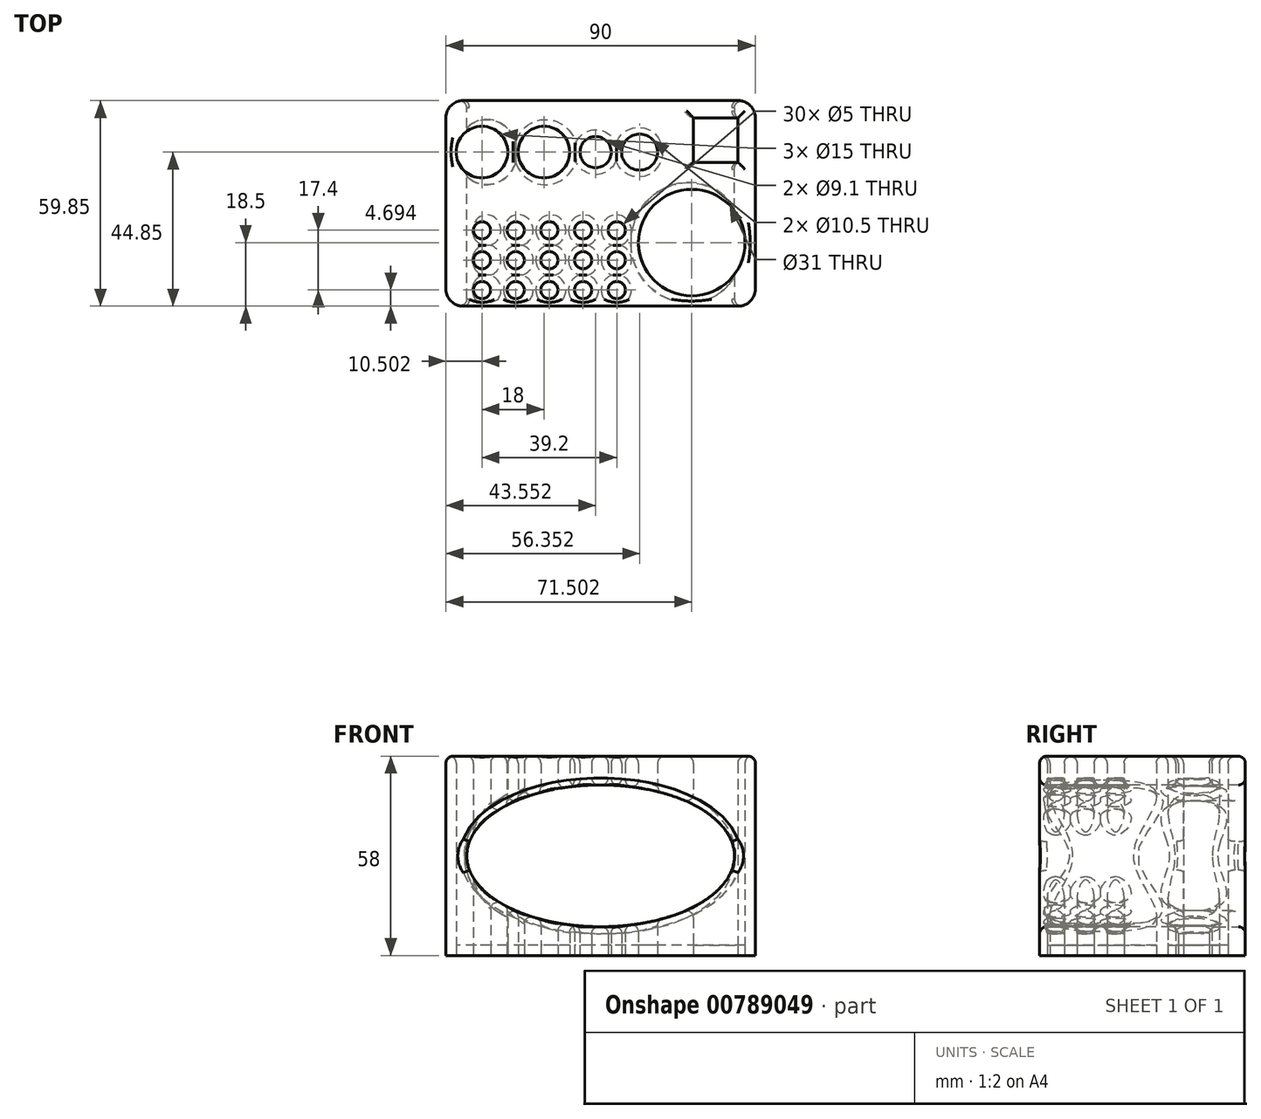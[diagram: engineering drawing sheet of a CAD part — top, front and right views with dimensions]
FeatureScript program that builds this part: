
annotation { "Feature Type Name" : "Feature", "Feature Type Description" : "" }
export const myFeature = defineFeature(function(context is Context, id is Id, definition is map)
    precondition{}
    {
        {
            var Q0;
            Q0=qCreatedBy(makeId("Top.planeOp"),FACE);
            var sketch = newSketch(context, id + "F0", { "sketchPlane" : qUnion([Q0])});
            skLineSegment(sketch, "E0.bottom", {"start": v(-28.22, 30.72) * mm, "end": v(51.78, 30.72) * mm});
            skLineSegment(sketch, "E0.top", {"start": v(-28.22, -29.13) * mm, "end": v(51.78, -29.13) * mm});
            skLineSegment(sketch, "E0.left", {"start": v(-33.22, 25.72) * mm, "end": v(-33.22, -24.13) * mm});
            skLineSegment(sketch, "E0.right", {"start": v(56.78, 25.72) * mm, "end": v(56.78, -24.13) * mm});
            skLineSegment(sketch, "E1.bottom", {"start": v(38.78, 25.72) * mm, "end": v(51.78, 25.72) * mm});
            skLineSegment(sketch, "E1.top", {"start": v(38.78, 12.72) * mm, "end": v(51.78, 12.72) * mm});
            skLineSegment(sketch, "E1.left", {"start": v(38.78, 25.72) * mm, "end": v(38.78, 12.72) * mm});
            skLineSegment(sketch, "E1.right", {"start": v(51.78, 25.72) * mm, "end": v(51.78, 12.72) * mm});
            skCircle(sketch, "E2", {"center": v(38.28, -10.63) * mm, "radius": 15.5 * mm});
            skCircle(sketch, "E3", {"center": v(-22.72, 15.72) * mm, "radius": 7.5 * mm});
            skCircle(sketch, "E4", {"center": v(-4.72, 15.72) * mm, "radius": 7.5 * mm});
            skLineSegment(sketch, "E5", {"start": v(-22.72, 15.72) * mm, "end": v(55.26, 15.72) * mm, "construction": true});
            skCircle(sketch, "E6", {"center": v(10.33, 15.72) * mm, "radius": 4.55 * mm});
            skCircle(sketch, "E7", {"center": v(23.13, 15.72) * mm, "radius": 5.25 * mm});
            skCircle(sketch, "E8", {"center": v(-22.72, -7.04) * mm, "radius": 2.5 * mm});
            skLineSegment(sketch, "E9", {"start": v(-22.72, 15.72) * mm, "end": v(-22.72, -24.26) * mm, "construction": true});
            skCircle(sketch, "E10.0.1.0", {"center": v(-22.72, -15.74) * mm, "radius": 2.5 * mm});
            skCircle(sketch, "E10.0.2.0", {"center": v(-22.72, -24.44) * mm, "radius": 2.5 * mm});
            skCircle(sketch, "E10.1.0.0", {"center": v(-12.92, -7.04) * mm, "radius": 2.5 * mm});
            skCircle(sketch, "E10.1.1.0", {"center": v(-12.92, -15.74) * mm, "radius": 2.5 * mm});
            skCircle(sketch, "E10.1.2.0", {"center": v(-12.92, -24.44) * mm, "radius": 2.5 * mm});
            skCircle(sketch, "E10.2.0.0", {"center": v(-3.12, -7.04) * mm, "radius": 2.5 * mm});
            skCircle(sketch, "E10.2.1.0", {"center": v(-3.12, -15.74) * mm, "radius": 2.5 * mm});
            skCircle(sketch, "E10.2.2.0", {"center": v(-3.12, -24.44) * mm, "radius": 2.5 * mm});
            skCircle(sketch, "E10.3.0.0", {"center": v(6.68, -7.04) * mm, "radius": 2.5 * mm});
            skCircle(sketch, "E10.3.1.0", {"center": v(6.68, -15.74) * mm, "radius": 2.5 * mm});
            skCircle(sketch, "E10.3.2.0", {"center": v(6.68, -24.44) * mm, "radius": 2.5 * mm});
            skCircle(sketch, "E10.4.0.0", {"center": v(16.48, -7.04) * mm, "radius": 2.5 * mm});
            skCircle(sketch, "E10.4.1.0", {"center": v(16.48, -15.74) * mm, "radius": 2.5 * mm});
            skCircle(sketch, "E10.4.2.0", {"center": v(16.48, -24.44) * mm, "radius": 2.5 * mm});
            skLineSegment(sketch, "E10.direction1", {"start": v(-22.72, -7.04) * mm, "end": v(-12.92, -7.04) * mm, "construction": true});
            skLineSegment(sketch, "E10.direction2", {"start": v(-22.72, -7.04) * mm, "end": v(-22.72, -15.74) * mm, "construction": true});
            skPoint(sketch, "E11.visualSharp", {"position": v(-33.22, 30.72) * mm});
            skArc(sketch, "E11.filletArc", {"start": v(-28.22, 30.72) * mm, "mid": v(-31.75, 29.26) * mm, "end": v(-33.22, 25.72) * mm});
            skPoint(sketch, "E12.visualSharp", {"position": v(56.78, 30.72) * mm});
            skArc(sketch, "E12.filletArc", {"start": v(56.78, 25.72) * mm, "mid": v(55.32, 29.26) * mm, "end": v(51.78, 30.72) * mm});
            skPoint(sketch, "E13.visualSharp", {"position": v(56.78, -29.13) * mm});
            skArc(sketch, "E13.filletArc", {"start": v(51.78, -29.13) * mm, "mid": v(55.32, -27.67) * mm, "end": v(56.78, -24.13) * mm});
            skPoint(sketch, "E14.visualSharp", {"position": v(-33.22, -29.13) * mm});
            skArc(sketch, "E14.filletArc", {"start": v(-33.22, -24.13) * mm, "mid": v(-31.75, -27.67) * mm, "end": v(-28.22, -29.13) * mm});
            skSolve(sketch);
        }
        {
            var Q0;
            Q0=makeQuery(id+"F0.imprint","IMPRINT",FACE,{"disambiguationData":[TD([[makeQuery(id+"F0.imprint","IMPRINT",EDGE,{"derivedFrom":sQuery(id+"F0.wireOp",EDGE,"E0.bottom")}),-1.0]])]});
            extrude(context, id + "F1", {"entities" : qUnion([Q0]), "depth" : 58 * mm, "offsetDistance" : 25 * mm});
        }
        {
            var Q0;
            Q0=makeQuery(id+"F0.imprint","IMPRINT",FACE,{"disambiguationData":[TD([[makeQuery(id+"F0.imprint","IMPRINT",EDGE,{"derivedFrom":sQuery(id+"F0.wireOp",EDGE,"E3")}),1.0]])]});
            var Q1;
            Q1=makeQuery(id+"F0.imprint","IMPRINT",FACE,{"disambiguationData":[TD([[makeQuery(id+"F0.imprint","IMPRINT",EDGE,{"derivedFrom":sQuery(id+"F0.wireOp",EDGE,"E4")}),1.0]])]});
            var Q2;
            Q2=makeQuery(id+"F0.imprint","IMPRINT",FACE,{"disambiguationData":[TD([[makeQuery(id+"F0.imprint","IMPRINT",EDGE,{"derivedFrom":sQuery(id+"F0.wireOp",EDGE,"E6")}),1.0]])]});
            var Q3;
            Q3=makeQuery(id+"F0.imprint","IMPRINT",FACE,{"disambiguationData":[TD([[makeQuery(id+"F0.imprint","IMPRINT",EDGE,{"derivedFrom":sQuery(id+"F0.wireOp",EDGE,"E7")}),1.0]])]});
            var Q4;
            Q4=makeQuery(id+"F0.imprint","IMPRINT",FACE,{"disambiguationData":[TD([[makeQuery(id+"F0.imprint","IMPRINT",EDGE,{"derivedFrom":sQuery(id+"F0.wireOp",EDGE,"E1.bottom")}),-1.0]])]});
            var Q5;
            Q5=makeQuery(id+"F0.imprint","IMPRINT",FACE,{"disambiguationData":[TD([[makeQuery(id+"F0.imprint","IMPRINT",EDGE,{"derivedFrom":sQuery(id+"F0.wireOp",EDGE,"E2")}),1.0]])]});
            var Q6;
            Q6=makeQuery(id+"F0.imprint","IMPRINT",FACE,{"disambiguationData":[TD([[makeQuery(id+"F0.imprint","IMPRINT",EDGE,{"derivedFrom":sQuery(id+"F0.wireOp",EDGE,"E10.4.0.0")}),1.0]])]});
            var Q7;
            Q7=makeQuery(id+"F0.imprint","IMPRINT",FACE,{"disambiguationData":[TD([[makeQuery(id+"F0.imprint","IMPRINT",EDGE,{"derivedFrom":sQuery(id+"F0.wireOp",EDGE,"E10.4.1.0")}),1.0]])]});
            var Q8;
            Q8=makeQuery(id+"F0.imprint","IMPRINT",FACE,{"disambiguationData":[TD([[makeQuery(id+"F0.imprint","IMPRINT",EDGE,{"derivedFrom":sQuery(id+"F0.wireOp",EDGE,"E10.4.2.0")}),1.0]])]});
            var Q9;
            Q9=makeQuery(id+"F0.imprint","IMPRINT",FACE,{"disambiguationData":[TD([[makeQuery(id+"F0.imprint","IMPRINT",EDGE,{"derivedFrom":sQuery(id+"F0.wireOp",EDGE,"E10.3.2.0")}),1.0]])]});
            var Q10;
            Q10=makeQuery(id+"F0.imprint","IMPRINT",FACE,{"disambiguationData":[TD([[makeQuery(id+"F0.imprint","IMPRINT",EDGE,{"derivedFrom":sQuery(id+"F0.wireOp",EDGE,"E10.3.1.0")}),1.0]])]});
            var Q11;
            Q11=makeQuery(id+"F0.imprint","IMPRINT",FACE,{"disambiguationData":[TD([[makeQuery(id+"F0.imprint","IMPRINT",EDGE,{"derivedFrom":sQuery(id+"F0.wireOp",EDGE,"E10.3.0.0")}),1.0]])]});
            var Q12;
            Q12=makeQuery(id+"F0.imprint","IMPRINT",FACE,{"disambiguationData":[TD([[makeQuery(id+"F0.imprint","IMPRINT",EDGE,{"derivedFrom":sQuery(id+"F0.wireOp",EDGE,"E10.2.0.0")}),1.0]])]});
            var Q13;
            Q13=makeQuery(id+"F0.imprint","IMPRINT",FACE,{"disambiguationData":[TD([[makeQuery(id+"F0.imprint","IMPRINT",EDGE,{"derivedFrom":sQuery(id+"F0.wireOp",EDGE,"E10.2.1.0")}),1.0]])]});
            var Q14;
            Q14=makeQuery(id+"F0.imprint","IMPRINT",FACE,{"disambiguationData":[TD([[makeQuery(id+"F0.imprint","IMPRINT",EDGE,{"derivedFrom":sQuery(id+"F0.wireOp",EDGE,"E10.2.2.0")}),1.0]])]});
            var Q15;
            Q15=makeQuery(id+"F0.imprint","IMPRINT",FACE,{"disambiguationData":[TD([[makeQuery(id+"F0.imprint","IMPRINT",EDGE,{"derivedFrom":sQuery(id+"F0.wireOp",EDGE,"E10.1.2.0")}),1.0]])]});
            var Q16;
            Q16=makeQuery(id+"F0.imprint","IMPRINT",FACE,{"disambiguationData":[TD([[makeQuery(id+"F0.imprint","IMPRINT",EDGE,{"derivedFrom":sQuery(id+"F0.wireOp",EDGE,"E10.1.1.0")}),1.0]])]});
            var Q17;
            Q17=makeQuery(id+"F0.imprint","IMPRINT",FACE,{"disambiguationData":[TD([[makeQuery(id+"F0.imprint","IMPRINT",EDGE,{"derivedFrom":sQuery(id+"F0.wireOp",EDGE,"E10.1.0.0")}),1.0]])]});
            var Q18;
            Q18=makeQuery(id+"F0.imprint","IMPRINT",FACE,{"disambiguationData":[TD([[makeQuery(id+"F0.imprint","IMPRINT",EDGE,{"derivedFrom":sQuery(id+"F0.wireOp",EDGE,"E8")}),1.0]])]});
            var Q19;
            Q19=makeQuery(id+"F0.imprint","IMPRINT",FACE,{"disambiguationData":[TD([[makeQuery(id+"F0.imprint","IMPRINT",EDGE,{"derivedFrom":sQuery(id+"F0.wireOp",EDGE,"E10.0.1.0")}),1.0]])]});
            var Q20;
            Q20=makeQuery(id+"F0.imprint","IMPRINT",FACE,{"disambiguationData":[TD([[makeQuery(id+"F0.imprint","IMPRINT",EDGE,{"derivedFrom":sQuery(id+"F0.wireOp",EDGE,"E10.0.2.0")}),1.0]])]});
            extrude(context, id + "F2", {"entities" : qUnion([Q0, Q1, Q2, Q3, Q4, Q5, Q6, Q7, Q8, Q9, Q10, Q11, Q12, Q13, Q14, Q15, Q16, Q17, Q18, Q19, Q20]), "depth" : 3 * mm, "offsetDistance" : 25 * mm});
        }
        {
            var Q0;
            Q0=makeQuery(id+"F1.opExtrude","SWEPT_FACE",FACE,{"disambiguationData":[OSD([sQuery(id+"F0.wireOp",EDGE,"E0.top")])]});
            var sketch = newSketch(context, id + "F3", { "sketchPlane" : qUnion([Q0])});
            skLineSegment(sketch, "E15", {"start": v(-28.22, 58) * mm, "end": v(51.78, 0) * mm, "construction": true});
            skEllipse(sketch, "E16", {"center": v(11.78, 29) * mm, "majorRadius": 20.64 * mm, "minorRadius": 38.94 * mm, "majorAxis": v(0, 1)});
            skSolve(sketch);
        }
        {
            var Q0;
            Q0 = qSketchRegion(id + "F3", true);
            var Q1;
            Q1=makeQuery(id+"F1.opExtrude","SWEPT_FACE",FACE,{"disambiguationData":[OSD([sQuery(id+"F0.wireOp",EDGE,"E0.bottom")])]});
            extrude(context, id + "F4", {"entities" : qUnion([Q0]), "operationType" : NewBodyOperationType.REMOVE, "endBound" : BoundingType.UP_TO_SURFACE, "oppositeDirection" : true, "depth" : 25 * mm, "endBoundEntityFace" : qUnion([Q1]), "offsetDistance" : 25 * mm});
        }
        {
            var Q0;
            Q0=makeQuery(id+"F4.boolean.opBoolean","COPY",FACE,{"derivedFrom":makeQuery(id+"F4.opExtrude","SWEPT_FACE",FACE,{"disambiguationData":[OSD([sQuery(id+"F3.wireOp",EDGE,"E16")])]})});
            var Q1;
            Q1=makeQuery(id+"F1.opExtrude","CAP_FACE",FACE,{"disambiguationData":[OSD([sQuery(id+"F0.wireOp",EDGE,"E0.bottom"),sQuery(id+"F0.wireOp",EDGE,"E0.top"),sQuery(id+"F0.wireOp",EDGE,"E0.left"),sQuery(id+"F0.wireOp",EDGE,"E0.right"),sQuery(id+"F0.wireOp",EDGE,"E1.bottom"),sQuery(id+"F0.wireOp",EDGE,"E1.top"),sQuery(id+"F0.wireOp",EDGE,"E1.left"),sQuery(id+"F0.wireOp",EDGE,"E1.right"),sQuery(id+"F0.wireOp",EDGE,"E2"),sQuery(id+"F0.wireOp",EDGE,"E3"),sQuery(id+"F0.wireOp",EDGE,"E4"),sQuery(id+"F0.wireOp",EDGE,"E6"),sQuery(id+"F0.wireOp",EDGE,"E7"),sQuery(id+"F0.wireOp",EDGE,"E8"),sQuery(id+"F0.wireOp",EDGE,"E10.0.1.0"),sQuery(id+"F0.wireOp",EDGE,"E10.0.2.0"),sQuery(id+"F0.wireOp",EDGE,"E10.1.0.0"),sQuery(id+"F0.wireOp",EDGE,"E10.1.1.0"),sQuery(id+"F0.wireOp",EDGE,"E10.1.2.0"),sQuery(id+"F0.wireOp",EDGE,"E10.2.0.0"),sQuery(id+"F0.wireOp",EDGE,"E10.2.1.0"),sQuery(id+"F0.wireOp",EDGE,"E10.2.2.0"),sQuery(id+"F0.wireOp",EDGE,"E10.3.0.0"),sQuery(id+"F0.wireOp",EDGE,"E10.3.1.0"),sQuery(id+"F0.wireOp",EDGE,"E10.3.2.0"),sQuery(id+"F0.wireOp",EDGE,"E10.4.0.0"),sQuery(id+"F0.wireOp",EDGE,"E10.4.1.0"),sQuery(id+"F0.wireOp",EDGE,"E10.4.2.0"),sQuery(id+"F0.wireOp",EDGE,"E11.filletArc"),sQuery(id+"F0.wireOp",EDGE,"E12.filletArc"),sQuery(id+"F0.wireOp",EDGE,"E13.filletArc"),sQuery(id+"F0.wireOp",EDGE,"E14.filletArc")])],"isStart":false});
            fillet(context, id + "F5", {"entities" : qUnion([Q0, Q1]), "radius" : 2 * mm, "tangentPropagation" : true, "allowEdgeOverflow" : false});
        }
    });
